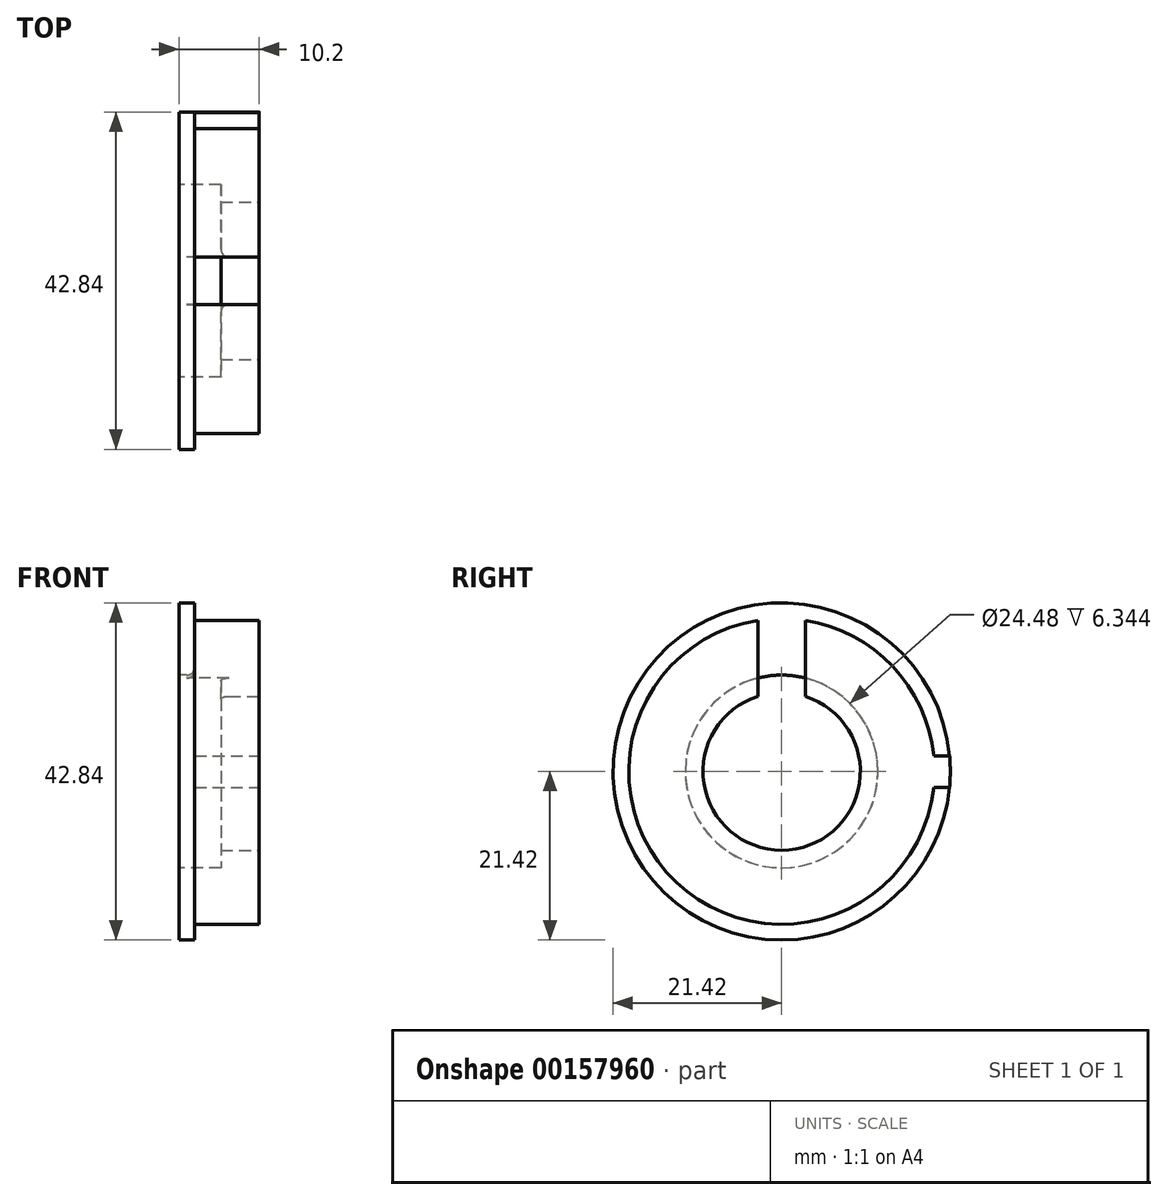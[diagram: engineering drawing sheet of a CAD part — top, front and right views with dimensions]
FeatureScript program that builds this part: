
annotation { "Feature Type Name" : "Feature", "Feature Type Description" : "" }
export const myFeature = defineFeature(function(context is Context, id is Id, definition is map)
    precondition{}
    {
        {
            var Q0;
            Q0=qCreatedBy(makeId("Right.planeOp"),FACE);
            var sketch = newSketch(context, id + "F0", { "sketchPlane" : qUnion([Q0])});
            skCircle(sketch, "E0", {"center": v(0, 0) * mm, "radius": 21.42 * mm});
            skSolve(sketch);
        }
        {
            var Q0;
            Q0=qSketchRegion(id+"F0",true);
            extrude(context, id + "F1", {"entities" : qUnion([Q0]), "oppositeDirection" : true, "depth" : 10.2 * mm});
        }
        {
            var Q0;
            Q0=makeQuery(id+"F1.opExtrude","CAP_FACE",FACE,{"disambiguationData":[OSD([sQuery(id+"F0.wireOp",EDGE,"E0")])],"isStart":true});
            var sketch = newSketch(context, id + "F2", { "sketchPlane" : qUnion([Q0])});
            skCircle(sketch, "E1", {"center": v(0, 0) * mm, "radius": 19.42 * mm});
            skLineSegment(sketch, "E2", {"start": v(19.32, -2) * mm, "end": v(21.33, -2) * mm});
            skLineSegment(sketch, "E3", {"start": v(19.32, 2) * mm, "end": v(21.33, 2) * mm});
            skSolve(sketch);
        }
        {
            var Q0;
            {var subQ0=sQuery(id+"F2.wireOp",EDGE,"E2");Q0=makeQuery(id+"F2.imprint","IMPRINT",FACE,{"disambiguationData":[TD([[makeQuery(id+"F2.imprint","IMPRINT",EDGE,{"derivedFrom":subQ0}),-1.0]])]});}
            extrude(context, id + "F3", {"entities" : qUnion([Q0]), "operationType" : NewBodyOperationType.REMOVE, "oppositeDirection" : true, "depth" : 8.2 * mm});
        }
        {
            var Q0;
            Q0=makeQuery(id+"F1.opExtrude","CAP_FACE",FACE,{"disambiguationData":[OSD([sQuery(id+"F0.wireOp",EDGE,"E0")])],"isStart":false});
            var sketch = newSketch(context, id + "F4", { "sketchPlane" : qUnion([Q0])});
            skCircle(sketch, "E4", {"center": v(0, 0) * mm, "radius": 12.24 * mm});
            skSolve(sketch);
        }
        {
            var Q0;
            Q0=makeQuery(id+"F4.imprint","IMPRINT",FACE,{"disambiguationData":[TD([[makeQuery(id+"F4.imprint","IMPRINT",EDGE,{"derivedFrom":sQuery(id+"F4.wireOp",EDGE,"E4")}),1.0]])]});
            extrude(context, id + "F5", {"entities" : qUnion([Q0]), "operationType" : NewBodyOperationType.REMOVE, "oppositeDirection" : true, "depth" : 5.34 * mm});
        }
        {
            var Q0;
            Q0=qCreatedBy(makeId("Top.planeOp"),FACE);
            var sketch = newSketch(context, id + "F6", { "sketchPlane" : qUnion([Q0])});
            skLineSegment(sketch, "E5.bottom", {"start": v(0, -3) * mm, "end": v(-8.2, -3) * mm});
            skLineSegment(sketch, "E5.top", {"start": v(0, 3) * mm, "end": v(-8.2, 3) * mm});
            skLineSegment(sketch, "E5.left", {"start": v(0, -3) * mm, "end": v(0, 3) * mm});
            skLineSegment(sketch, "E5.right", {"start": v(-8.2, -3) * mm, "end": v(-8.2, 3) * mm});
            skSolve(sketch);
        }
        {
            var Q0;
            Q0=qSketchRegion(id+"F6",true);
            extrude(context, id + "F7", {"entities" : qUnion([Q0]), "operationType" : NewBodyOperationType.REMOVE, "depth" : 25 * mm});
        }
        {
            var Q0;
            Q0=makeQuery(id+"F1TqEJiA9k82aoi_1.boolean.opBoolean","COPY",EDGE,{"derivedFrom":makeQuery(id+"F1TqEJiA9k82aoi_1.opExtrude","CAP_EDGE",EDGE,{"disambiguationData":[OSD([sQuery(id+"FNwscczDqfitw4l_1.wireOp",EDGE,"hiqOlHvr-swhN-U5Gd-yb4O-lsnh0rtTb3Ss.right")])],"isStart":true})});
            var Q1;
            Q1=makeQuery(id+"F1TqEJiA9k82aoi_1.boolean.opBoolean","COPY",EDGE,{"derivedFrom":makeQuery(id+"F1TqEJiA9k82aoi_1.opExtrude","CAP_EDGE",EDGE,{"disambiguationData":[OSD([sQuery(id+"FNwscczDqfitw4l_1.wireOp",EDGE,"hiqOlHvr-swhN-U5Gd-yb4O-lsnh0rtTb3Ss.bottom")])],"isStart":true})});
            var Q2;
            Q2=makeQuery(id+"F1TqEJiA9k82aoi_1.boolean.opBoolean","COPY",EDGE,{"derivedFrom":makeQuery(id+"F1TqEJiA9k82aoi_1.opExtrude","CAP_EDGE",EDGE,{"disambiguationData":[OSD([sQuery(id+"FNwscczDqfitw4l_1.wireOp",EDGE,"hiqOlHvr-swhN-U5Gd-yb4O-lsnh0rtTb3Ss.left")])],"isStart":true})});
            var Q3;
            Q3=makeQuery(id+"F1TqEJiA9k82aoi_1.boolean.opBoolean","COPY",EDGE,{"derivedFrom":makeQuery(id+"F1TqEJiA9k82aoi_1.opExtrude","CAP_EDGE",EDGE,{"disambiguationData":[OSD([sQuery(id+"FNwscczDqfitw4l_1.wireOp",EDGE,"hiqOlHvr-swhN-U5Gd-yb4O-lsnh0rtTb3Ss.top")])],"isStart":true})});
            var Q4;
            Q4=makeQuery(id+"F7.boolean.opBoolean","INTERSECT",EDGE,{"derivedFrom":[makeQuery(id+"F5.boolean.opBoolean","COPY",FACE,{"derivedFrom":makeQuery(id+"F5.opExtrude","CAP_FACE",FACE,{"disambiguationData":[OSD([sQuery(id+"F4.wireOp",EDGE,"E4")])],"isStart":false})}),makeQuery(id+"F7.opExtrude","SWEPT_FACE",FACE,{"disambiguationData":[OSD([sQuery(id+"F6.wireOp",EDGE,"E5.top")])]})]});
            var Q5;
            Q5=makeQuery(id+"F7.boolean.opBoolean","INTERSECT",EDGE,{"derivedFrom":[makeQuery(id+"F5.boolean.opBoolean","COPY",FACE,{"derivedFrom":makeQuery(id+"F5.opExtrude","CAP_FACE",FACE,{"disambiguationData":[OSD([sQuery(id+"F4.wireOp",EDGE,"E4")])],"isStart":false})}),makeQuery(id+"F7.opExtrude","SWEPT_FACE",FACE,{"disambiguationData":[OSD([sQuery(id+"F6.wireOp",EDGE,"E5.bottom")])]})]});
            var Q6;
            Q6=makeQuery(id+"F7.boolean.opBoolean","INTERSECT",EDGE,{"derivedFrom":[makeQuery(id+"F5.boolean.opBoolean","COPY",FACE,{"derivedFrom":makeQuery(id+"F5.opExtrude","SWEPT_FACE",FACE,{"disambiguationData":[OSD([sQuery(id+"F4.wireOp",EDGE,"E4")])]})}),makeQuery(id+"F7.opExtrude","SWEPT_FACE",FACE,{"disambiguationData":[OSD([sQuery(id+"F6.wireOp",EDGE,"E5.right")])]})]});
            fillet(context, id + "F8", {"entities" : qUnion([Q0, Q1, Q2, Q3, Q4, Q5, Q6]), "radius" : 1 * mm, "tangentPropagation" : true, "allowEdgeOverflow" : false});
        }
        {
            var Q0;
            Q0=makeQuery(id+"F1.opExtrude","CAP_FACE",FACE,{"disambiguationData":[OSD([sQuery(id+"F0.wireOp",EDGE,"E0")])],"isStart":true});
            var sketch = newSketch(context, id + "F9", { "sketchPlane" : qUnion([Q0])});
            skCircle(sketch, "E6", {"center": v(0, 0) * mm, "radius": 10 * mm});
            skSolve(sketch);
        }
        {
            var Q0;
            Q0=qSketchRegion(id+"F9",true);
            extrude(context, id + "F10", {"entities" : qUnion([Q0]), "operationType" : NewBodyOperationType.REMOVE, "oppositeDirection" : true, "depth" : 6 * mm});
        }
    });
